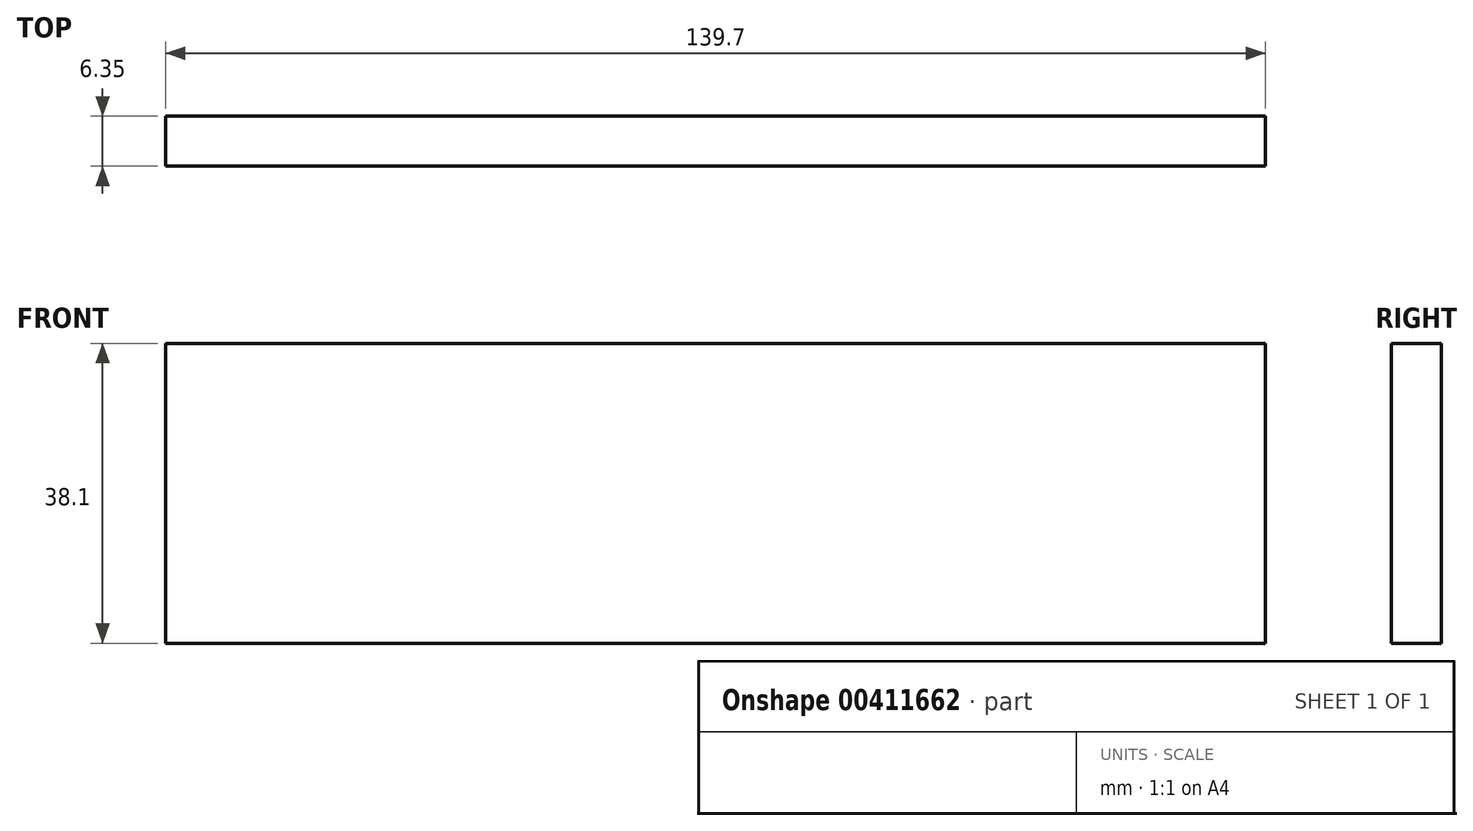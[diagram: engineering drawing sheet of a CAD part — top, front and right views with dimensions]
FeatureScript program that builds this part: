
annotation { "Feature Type Name" : "Feature", "Feature Type Description" : "" }
export const myFeature = defineFeature(function(context is Context, id is Id, definition is map)
    precondition{}
    {
        {
            var Q0;
            Q0=qCreatedBy(makeId("Top.planeOp"),FACE);
            var sketch = newSketch(context, id + "F0", { "sketchPlane" : qUnion([Q0])});
            skLineSegment(sketch, "E0.bottom", {"start": v(0, -14.02) * mm, "end": v(139.7, -14.02) * mm});
            skLineSegment(sketch, "E0.top", {"start": v(0, -20.37) * mm, "end": v(139.7, -20.37) * mm});
            skLineSegment(sketch, "E0.left", {"start": v(0, -14.02) * mm, "end": v(0, -20.37) * mm});
            skLineSegment(sketch, "E0.right", {"start": v(139.7, -14.02) * mm, "end": v(139.7, -20.37) * mm});
            skSolve(sketch);
        }
        {
            var Q0;
            Q0=makeQuery(id+"F0.imprint","IMPRINT",FACE,{"disambiguationData":[TD([[makeQuery(id+"F0.imprint","IMPRINT",EDGE,{"derivedFrom":sQuery(id+"F0.wireOp",EDGE,"E0.bottom")}),-1.0]])]});
            extrude(context, id + "F1", {"entities" : qUnion([Q0]), "depth" : 38.1 * mm});
        }
    });
